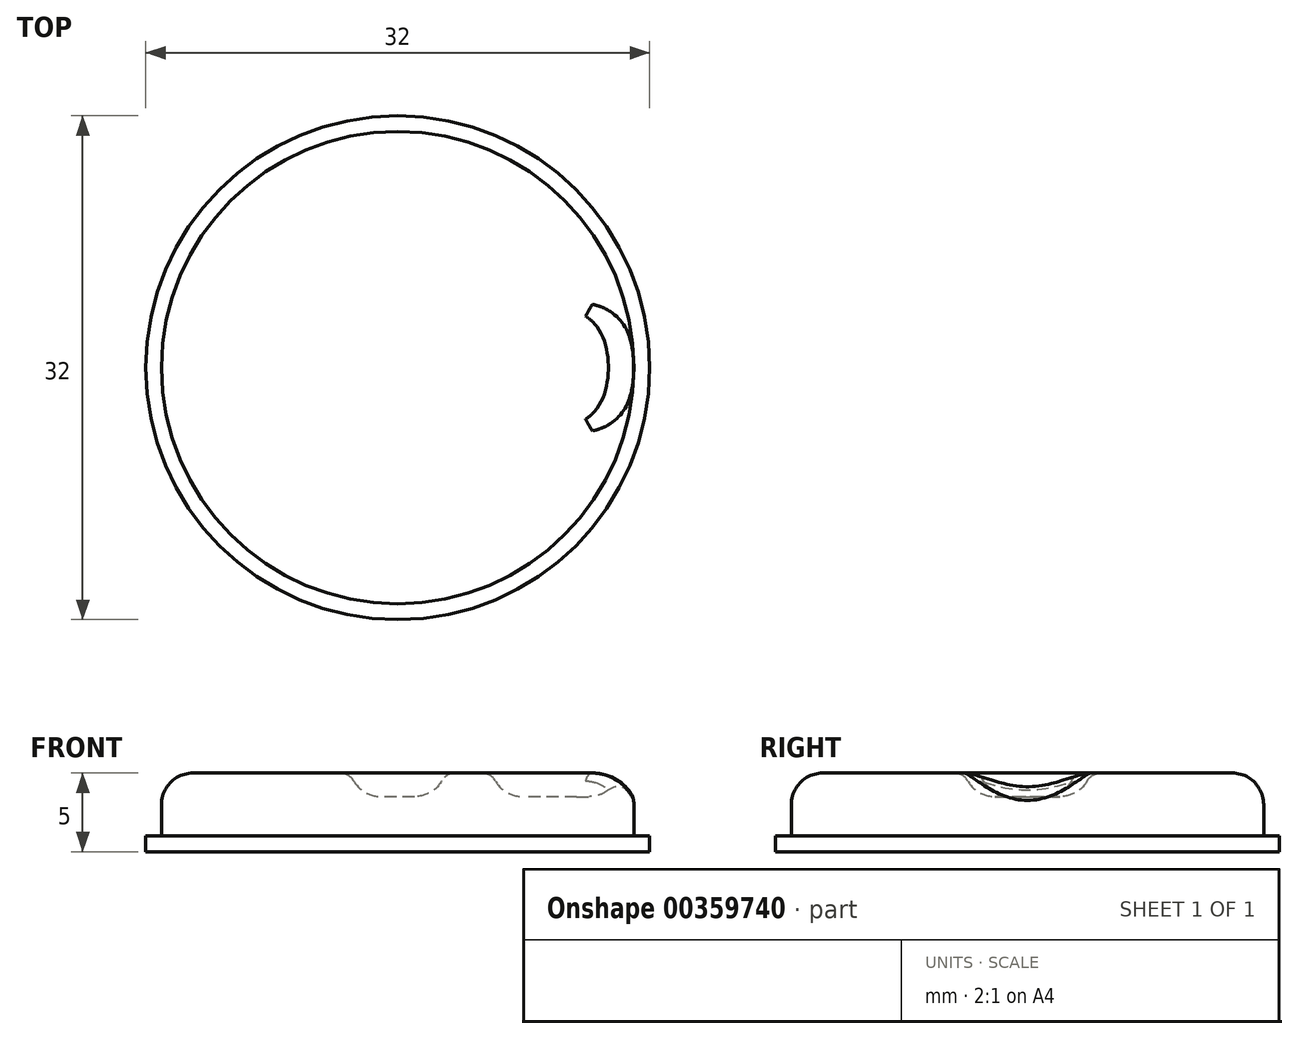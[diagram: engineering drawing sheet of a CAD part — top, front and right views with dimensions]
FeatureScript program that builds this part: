
annotation { "Feature Type Name" : "Feature", "Feature Type Description" : "" }
export const myFeature = defineFeature(function(context is Context, id is Id, definition is map)
    precondition{}
    {
        {
            var Q0;
            Q0=qCreatedBy(makeId("Top.planeOp"),FACE);
            var sketch = newSketch(context, id + "F0", { "sketchPlane" : qUnion([Q0])});
            skCircle(sketch, "E0", {"center": v(0, 0) * mm, "radius": 15 * mm});
            skCircle(sketch, "E1", {"center": v(0, 0) * mm, "radius": 10 * mm, "construction": true});
            skCircle(sketch, "E2", {"center": v(10, 0) * mm, "radius": 4 * mm});
            skCircle(sketch, "E3", {"center": v(0, 0) * mm, "radius": 3 * mm});
            skSolve(sketch);
        }
        {
            var Q0;
            Q0 = qSketchRegion(id + "F0", true);
            var Q1;
            Q1=makeQuery(id+"F0.imprint","IMPRINT",FACE,{"disambiguationData":[TD([[makeQuery(id+"F0.imprint","IMPRINT",EDGE,{"derivedFrom":sQuery(id+"F0.wireOp",EDGE,"E2")}),1.0]])]});
            var Q2;
            Q2=makeQuery(id+"F0.imprint","IMPRINT",FACE,{"disambiguationData":[TD([[makeQuery(id+"F0.imprint","IMPRINT",EDGE,{"derivedFrom":sQuery(id+"F0.wireOp",EDGE,"E3")}),1.0]])]});
            extrude(context, id + "F1", {"entities" : qUnion([Q0, Q1, Q2]), "oppositeDirection" : true, "depth" : 5 * mm});
        }
        {
            var Q0;
            Q0=makeQuery(id+"F1.opExtrude","CAP_EDGE",EDGE,{"disambiguationData":[OSD([sQuery(id+"F0.wireOp",EDGE,"E0")])],"isStart":true});
            fillet(context, id + "F2", {"entities" : qUnion([Q0]), "radius" : 2 * mm, "tangentPropagation" : true, "allowEdgeOverflow" : false});
        }
        {
            var Q0;
            Q0=makeQuery(id+"F0.imprint","IMPRINT",FACE,{"disambiguationData":[TD([[makeQuery(id+"F0.imprint","IMPRINT",EDGE,{"derivedFrom":sQuery(id+"F0.wireOp",EDGE,"E3")}),1.0]])]});
            var Q1;
            Q1=makeQuery(id+"F0.imprint","IMPRINT",FACE,{"disambiguationData":[TD([[makeQuery(id+"F0.imprint","IMPRINT",EDGE,{"derivedFrom":sQuery(id+"F0.wireOp",EDGE,"E2")}),1.0]])]});
            extrude(context, id + "F3", {"entities" : qUnion([Q0, Q1]), "operationType" : NewBodyOperationType.REMOVE, "oppositeDirection" : true, "depth" : 1.5 * mm});
        }
        {
            var Q0;
            Q0=makeQuery(id+"F3.boolean.opBoolean","COPY",EDGE,{"derivedFrom":makeQuery(id+"F3.opExtrude","CAP_EDGE",EDGE,{"disambiguationData":[OSD([sQuery(id+"F0.wireOp",EDGE,"E3")])],"isStart":false})});
            var Q1;
            Q1=makeQuery(id+"F3.boolean.opBoolean","COPY",EDGE,{"derivedFrom":makeQuery(id+"F3.opExtrude","CAP_EDGE",EDGE,{"disambiguationData":[OSD([sQuery(id+"F0.wireOp",EDGE,"E2")])],"isStart":false})});
            fillet(context, id + "F4", {"entities" : qUnion([Q0, Q1]), "radius" : 2 * mm, "tangentPropagation" : true, "allowEdgeOverflow" : false});
        }
        {
            var Q0;
            Q0=makeQuery(id+"F4.opFillet","BLEND_EDGE",EDGE,{"blendedFrom":[makeQuery(id+"F3.boolean.opBoolean","COPY",EDGE,{"derivedFrom":makeQuery(id+"F3.opExtrude","CAP_EDGE",EDGE,{"disambiguationData":[OSD([sQuery(id+"F0.wireOp",EDGE,"E2")])],"isStart":false})}),makeQuery(id+"F1.opExtrude","CAP_FACE",FACE,{"disambiguationData":[OSD([sQuery(id+"F0.wireOp",EDGE,"E0")])],"isStart":true})],"blendedInto":[makeQuery(id+"F1.opExtrude","CAP_FACE",FACE,{"disambiguationData":[OSD([sQuery(id+"F0.wireOp",EDGE,"E0")])],"isStart":true})]});
            fillet(context, id + "F5", {"entities" : qUnion([Q0]), "radius" : 1 * mm, "tangentPropagation" : true, "allowEdgeOverflow" : false});
        }
        {
            var Q0;
            Q0=makeQuery(id+"F4.opFillet","BLEND_EDGE",EDGE,{"blendedFrom":[makeQuery(id+"F3.boolean.opBoolean","COPY",EDGE,{"derivedFrom":makeQuery(id+"F3.opExtrude","CAP_EDGE",EDGE,{"disambiguationData":[OSD([sQuery(id+"F0.wireOp",EDGE,"E3")])],"isStart":false})}),makeQuery(id+"F1.opExtrude","CAP_FACE",FACE,{"disambiguationData":[OSD([sQuery(id+"F0.wireOp",EDGE,"E0")])],"isStart":true})],"blendedInto":[makeQuery(id+"F1.opExtrude","CAP_FACE",FACE,{"disambiguationData":[OSD([sQuery(id+"F0.wireOp",EDGE,"E0")])],"isStart":true})]});
            fillet(context, id + "F6", {"entities" : qUnion([Q0]), "radius" : 1 * mm, "tangentPropagation" : true, "allowEdgeOverflow" : false});
        }
        {
            var Q0;
            Q0=makeQuery(id+"F1.opExtrude","CAP_FACE",FACE,{"disambiguationData":[OSD([sQuery(id+"F0.wireOp",EDGE,"E0")])],"isStart":false});
            var sketch = newSketch(context, id + "F7", { "sketchPlane" : qUnion([Q0])});
            skPoint(sketch, "E4.0", {"position": v(0, 0) * mm});
            skCircle(sketch, "E4.1", {"center": v(0, 0) * mm, "radius": 3 * mm});
            skCircle(sketch, "E5", {"center": v(0, 0) * mm, "radius": 16 * mm});
            skSolve(sketch);
        }
        {
            var Q0;
            Q0 = qSketchRegion(id + "F7", true);
            extrude(context, id + "F8", {"entities" : qUnion([Q0]), "operationType" : NewBodyOperationType.ADD, "oppositeDirection" : true, "depth" : 1 * mm});
        }
    });
